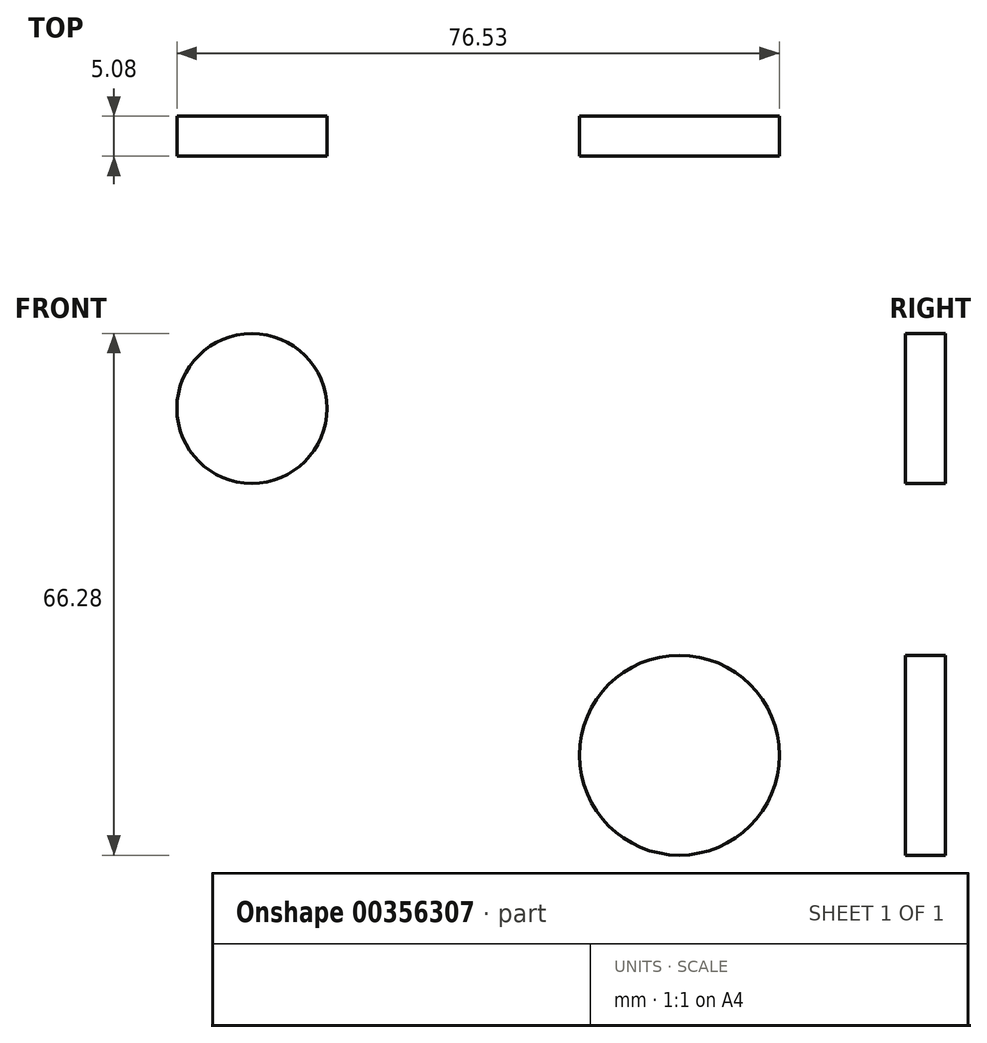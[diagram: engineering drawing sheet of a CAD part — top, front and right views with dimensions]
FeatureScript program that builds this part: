
annotation { "Feature Type Name" : "Feature", "Feature Type Description" : "" }
export const myFeature = defineFeature(function(context is Context, id is Id, definition is map)
    precondition{}
    {
        {
            var Q0;
            Q0=qCreatedBy(makeId("Front.planeOp"),FACE);
            var sketch = newSketch(context, id + "F0", { "sketchPlane" : qUnion([Q0])});
            skCircle(sketch, "E0", {"center": v(0, 0) * mm, "radius": 12.7 * mm});
            skSolve(sketch);
        }
        {
            var Q0;
            Q0=makeQuery(id+"F0.imprint","IMPRINT",FACE,{"disambiguationData":[TD([[makeQuery(id+"F0.imprint","IMPRINT",EDGE,{"derivedFrom":sQuery(id+"F0.wireOp",EDGE,"E0")}),1.0]])]});
            extrude(context, id + "F1", {"entities" : qUnion([Q0]), "depth" : 5.08 * mm});
        }
        {
            var Q0;
            Q0=qCreatedBy(makeId("Front.planeOp"),FACE);
            var sketch = newSketch(context, id + "F2", { "sketchPlane" : qUnion([Q0])});
            skCircle(sketch, "E1", {"center": v(-54.3, 44.05) * mm, "radius": 9.53 * mm});
            skSolve(sketch);
        }
        {
            var Q0;
            Q0=qSketchRegion(id+"F2",true);
            extrude(context, id + "F3", {"entities" : qUnion([Q0]), "depth" : 5.08 * mm});
        }
    });
